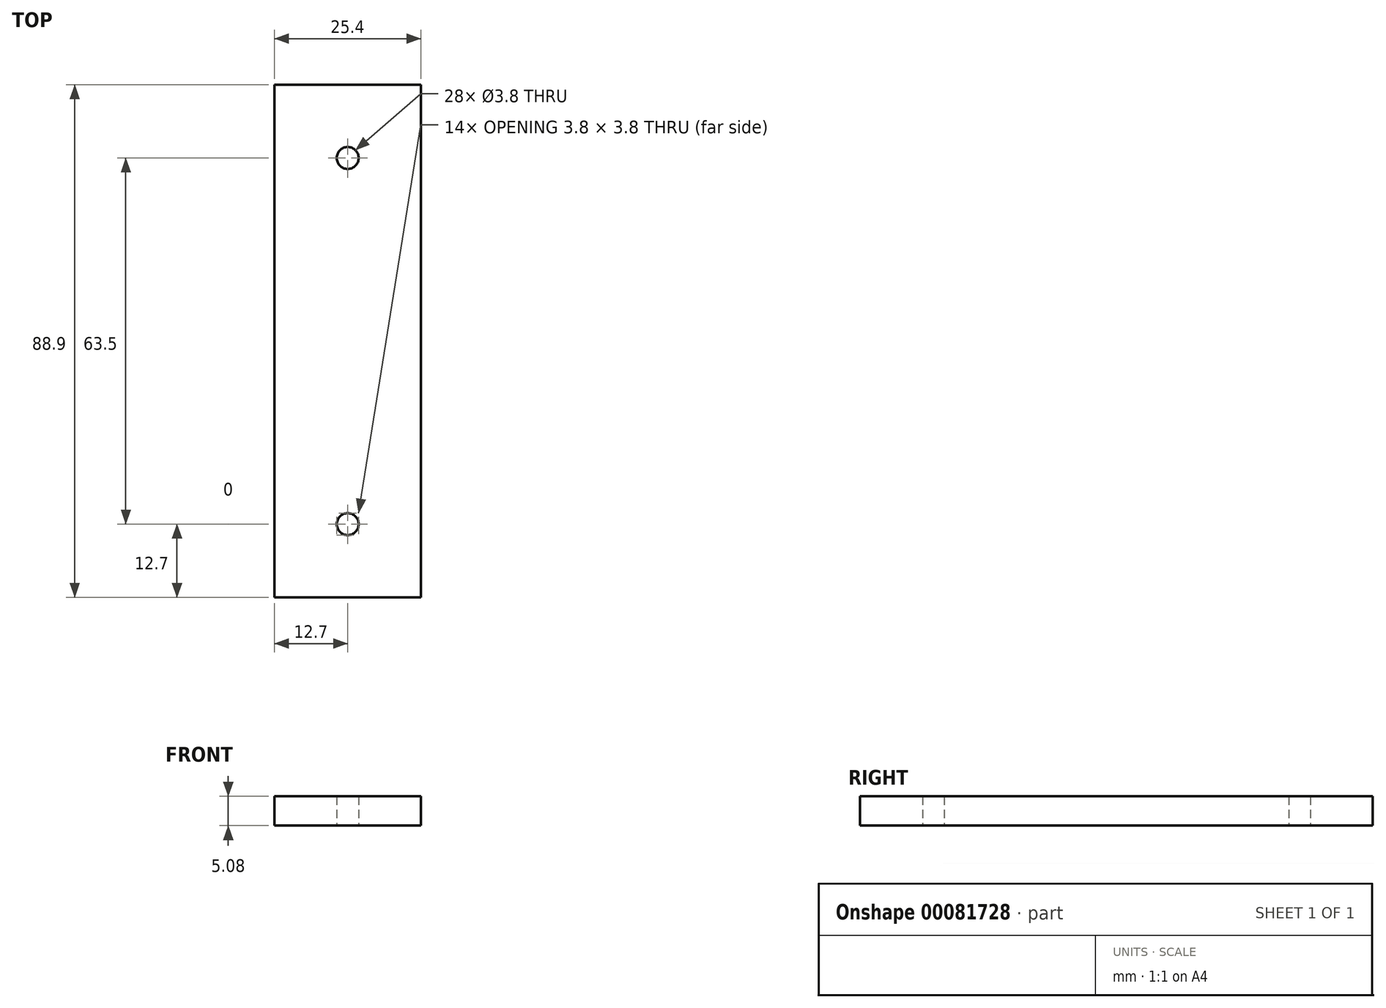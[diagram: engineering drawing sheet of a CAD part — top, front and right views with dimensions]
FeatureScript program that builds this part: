
annotation { "Feature Type Name" : "Feature", "Feature Type Description" : "" }
export const myFeature = defineFeature(function(context is Context, id is Id, definition is map)
    precondition{}
    {
        {
            var Q0;
            Q0=qCreatedBy(makeId("Top.planeOp"),FACE);
            var sketch = newSketch(context, id + "F0", { "sketchPlane" : qUnion([Q0])});
            skLineSegment(sketch, "E0.bottom", {"start": v(0, 0) * mm, "end": v(25.4, 0) * mm});
            skLineSegment(sketch, "E0.top", {"start": v(0, 88.9) * mm, "end": v(25.4, 88.9) * mm});
            skLineSegment(sketch, "E0.left", {"start": v(0, 0) * mm, "end": v(0, 88.9) * mm});
            skLineSegment(sketch, "E0.right", {"start": v(25.4, 0) * mm, "end": v(25.4, 88.9) * mm});
            skSolve(sketch);
        }
        {
            var Q0;
            Q0 = qSketchRegion(id + "F0", true);
            extrude(context, id + "F1", {"entities" : qUnion([Q0]), "depth" : 5.08 * mm});
        }
        {
            var Q0;
            Q0=makeQuery(id+"F1.opExtrude","CAP_FACE",FACE,{"disambiguationData":[OSD([sQuery(id+"F0.wireOp",EDGE,"E0.bottom"),sQuery(id+"F0.wireOp",EDGE,"E0.top"),sQuery(id+"F0.wireOp",EDGE,"E0.left"),sQuery(id+"F0.wireOp",EDGE,"E0.right")])],"isStart":false});
            var sketch = newSketch(context, id + "F2", { "sketchPlane" : qUnion([Q0])});
            skPoint(sketch, "E1", {"position": v(12.7, 76.2) * mm});
            skPoint(sketch, "E2", {"position": v(12.7, 12.7) * mm});
            skSolve(sketch);
        }
        {
            var Q0;
            Q0=sQuery(id+"F2.wireOp",VERTEX,"E1");
            var Q1;
            Q1=sQuery(id+"F2.wireOp",VERTEX,"E2");
            var Q2;
            Q2=makeQuery(id+"F1.opExtrude","SWEPT_BODY",BODY,{"disambiguationData":[OSD([sQuery(id+"F0.wireOp",EDGE,"E0.bottom"),sQuery(id+"F0.wireOp",EDGE,"E0.top"),sQuery(id+"F0.wireOp",EDGE,"E0.left"),sQuery(id+"F0.wireOp",EDGE,"E0.right")])]});
            hole(context, id + "F3", {"style" : HoleStyle.SIMPLE, "endStyle" : HoleEndStyle.THROUGH, "standardTappedOrClearance" : lookupTablePath({ "standard" : "ANSI", "fit" : "Normal (ASME)", "size" : "#6", "type" : "Clearance" }), "standardBlindInLast" : lookupTablePath({ "fit" : "Free", "standard" : "ANSI", "size" : "#6", "type" : "Clearance" }), "holeDiameter" : 3.8 * mm, "locations" : qUnion([Q0, Q1]), "scope" : qUnion([Q2]), "isTappedThrough" : true, "startStyle" : HoleStartStyle.PART});
        }
    });
